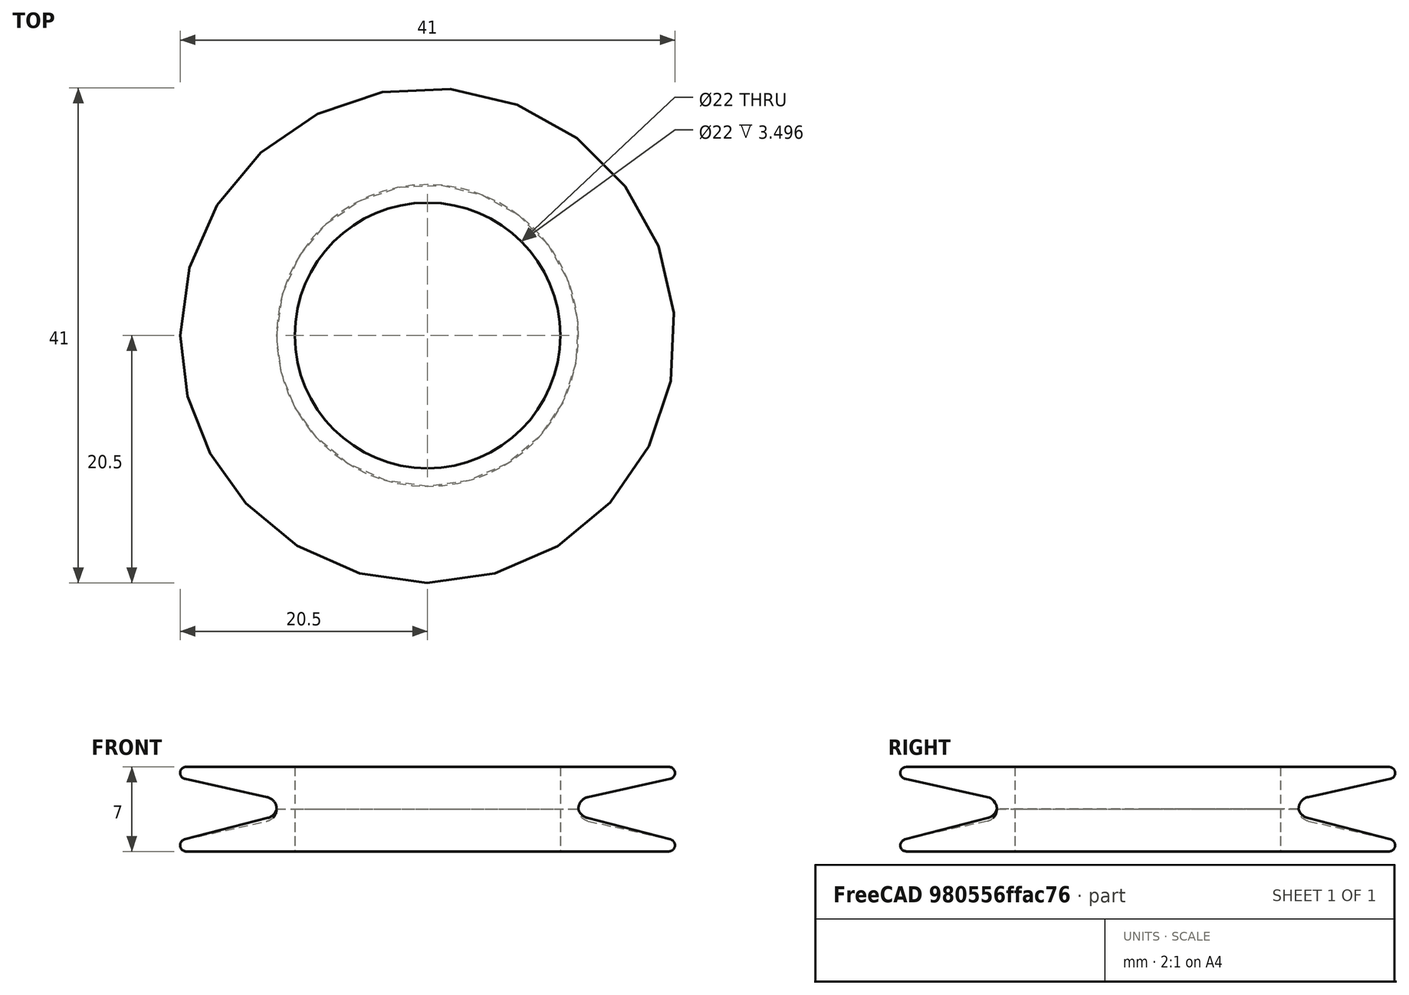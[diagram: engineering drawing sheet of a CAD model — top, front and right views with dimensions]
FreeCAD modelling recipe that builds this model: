
FCSTD DOCUMENT  (FreeCAD 0.18R4 (GitTag))
Label: Ring_BIG
License: All rights reserved
LicenseURL: http://en.wikipedia.org/wiki/All_rights_reserved
objects: Sketcher::SketchObject×2, PartDesign::Revolution×2, PartDesign::Body×2, App::Part×2
note: 8 computed .brp shape members not serialized (recipe doc carries the construction recipe); baked Part::Feature solids carry a one-line shape summary decoded from their .brp

FEATURE [Sketcher::SketchObject] Sketch002
  Placement = pos=(0,0,0) rot=(1,0,0;1.5708rad)
  Support = -> [XY_Plane]
  sketch-geometry (12):
    g0: LineSegment StartX=-11 StartY=7 StartZ=0 EndX=-11 EndY=0 EndZ=0
    g1: LineSegment StartX=-20.1091 StartY=0.987946 StartZ=0 EndX=-13.3034 EndY=2.51 EndZ=0
    g2: LineSegment StartX=-13.3034 StartY=4.51 StartZ=0 EndX=-20.1078 EndY=6.01175 EndZ=0
    g3: LineSegment StartX=-20 StartY=7 StartZ=0 EndX=-11 EndY=7 EndZ=0
    g4: ArcOfCircle CenterX=-20 CenterY=0.5 CenterZ=0 NormalX=0 NormalY=0 NormalZ=1 AngleXU=0 Radius=0.5 StartAngle=1.79082 EndAngle=4.7119
    g5: LineSegment [constr] StartX=-18.7772 StartY=3.51 StartZ=0 EndX=1.49954 EndY=3.51 EndZ=0
    g6: ArcOfCircle CenterX=-20 CenterY=6.5 CenterZ=0 NormalX=0 NormalY=0 NormalZ=1 AngleXU=0 Radius=0.5 StartAngle=1.5708 EndAngle=4.49517
    g7: LineSegment [constr] StartX=-20 StartY=6.5 StartZ=0 EndX=0 EndY=6.5 EndZ=0
    g8: LineSegment [constr] StartX=-20 StartY=0.5 StartZ=0 EndX=0 EndY=0.5 EndZ=0
    g9: ArcOfCircle CenterX=-13.5241 CenterY=3.51 CenterZ=0 NormalX=0 NormalY=0 NormalZ=1 AngleXU=0 Radius=1.02407 StartAngle=4.92961 EndAngle=7.63676
    g10: GeomPoint X=-12.5 Y=3.51 Z=0
    g11: LineSegment StartX=-20.0002 StartY=0 StartZ=0 EndX=-11 EndY=0 EndZ=0
  constraints (3):
    c: Coincident(g11,g4)
    c: Coincident(g11,g0)
    c: Horizontal(g11)
FEATURE [PartDesign::Revolution] Revolution
  Angle = 360
  Axis = (0,-2e-16,1)
  Base = (0,0,0)
  Profile = -> Sketch002
  ReferenceAxis = -> Sketch002 [V_Axis]
FEATURE [PartDesign::Body] Body
  Group = -> [Sketch002,Revolution]
  Origin = -> Origin001
  Tip = -> Revolution
FEATURE [App::Part] Part  label="Ring without splitting (not used)"
  Group = -> [Body]
  Origin = -> Origin
FEATURE [Sketcher::SketchObject] Sketch003
  Placement = pos=(0,0,0) rot=(1,0,0;1.5708rad)
  Support = -> [XY_Plane002]
  sketch-geometry (9):
    g0: LineSegment StartX=-11 StartY=3.5 StartZ=0 EndX=-11 EndY=0.00417483 EndZ=0
    g1: LineSegment StartX=-20.1253 StartY=0.988406 StartZ=0 EndX=-13.2328 EndY=2.77255 EndZ=0
    g2: ArcOfCircle CenterX=-20 CenterY=0.504269 CenterZ=0 NormalX=0 NormalY=0 NormalZ=1 AngleXU=0 Radius=0.500094 StartAngle=1.82409 EndAngle=4.7119
    g3: LineSegment [constr] StartX=-18.7772 StartY=3.5 StartZ=0 EndX=0 EndY=3.5 EndZ=0
    g4: LineSegment [constr] StartX=-20 StartY=0.5 StartZ=0 EndX=0 EndY=0.5 EndZ=0
    g5: ArcOfCircle CenterX=-13.4894 CenterY=3.76387 CenterZ=0 NormalX=0 NormalY=0 NormalZ=1 AngleXU=0 Radius=1.024 StartAngle=4.96568 EndAngle=6.02256
    g6: GeomPoint X=-12.5 Y=3.5 Z=0
    g7: LineSegment StartX=-20.0002 StartY=0.00417483 StartZ=0 EndX=-11 EndY=0.00417483 EndZ=0
    g8: LineSegment StartX=-12.5 StartY=3.5 StartZ=0 EndX=-11 EndY=3.5 EndZ=0
  constraints (17):
    c: Coincident(g7,g2)
    c: Coincident(g7,g0)
    c: Horizontal(g7)
    c: DistanceX(g0) = -11
    c: PointOnObject(g3,g-2)
    c: DistanceY(g3) = 3.5
    c: Horizontal(g3)
    c: PointOnObject(g0,g3)
    c: Radius(g5) = 1.024
    c: DistanceX(g6,g0) = 1.5
    c: Vertical(g0)
    c: Coincident(g5,g6)
    c: Tangent(g5,g1) = -1.5708
    c: PointOnObject(g5,g3)
    c: Coincident(g8,g5)
    c: Coincident(g8,g0)
    c: Tangent(g2,g1) = 1.5708
FEATURE [PartDesign::Revolution] Revolution001
  Angle = 360
  Axis = (0,2e-16,1)
  Base = (0,0,0)
  Profile = -> Sketch003
  ReferenceAxis = -> Sketch003 [V_Axis]
FEATURE [PartDesign::Body] Body001
  Group = -> [Sketch003,Revolution001]
  Origin = -> Origin003
  Tip = -> Revolution001
FEATURE [App::Part] Part001  label="Split Ring (half)"
  Group = -> [Body001]
  Origin = -> Origin002
